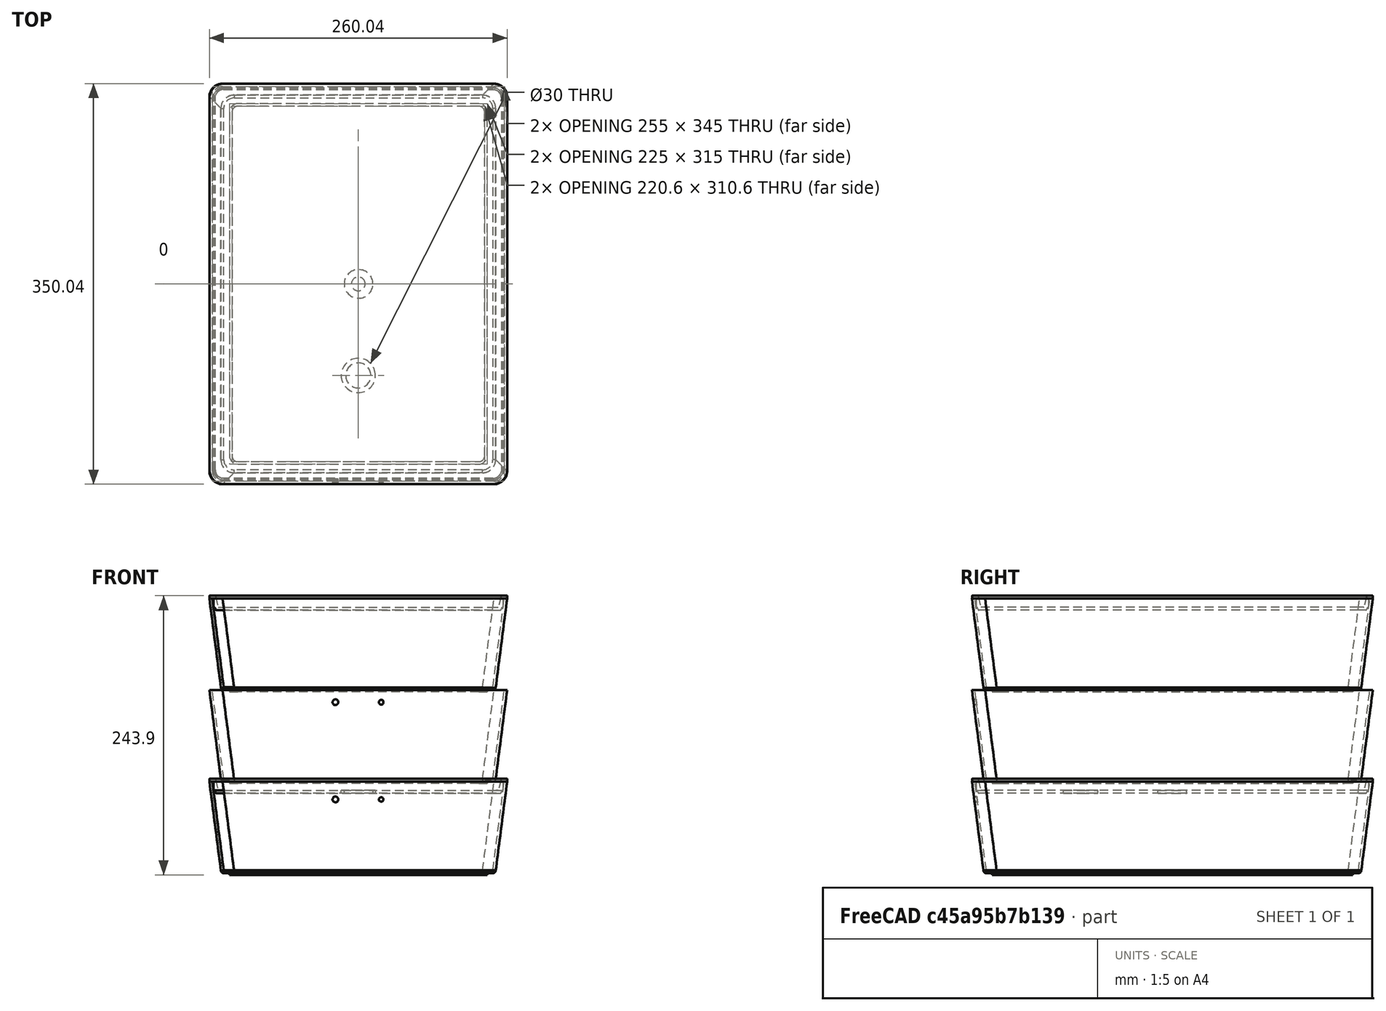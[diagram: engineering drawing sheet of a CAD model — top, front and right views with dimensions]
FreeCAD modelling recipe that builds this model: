
FCSTD DOCUMENT  (FreeCAD 0.16R6707 (Git))
Label: kuggis
License: All rights reserved
LicenseURL: http://en.wikipedia.org/wiki/All_rights_reserved
objects: Sketcher::SketchObject×10, Part::FeaturePython×6, PartDesign::Pad×3, Mesh::Feature×3, PartDesign::Pocket×3, Part::Feature×2, App::DocumentObjectGroup×2, Part::Cut×2, Part::Loft×1, Part::Thickness×1, Part::Sweep×1, Part::MultiFuse×1
note: 36 computed .brp shape members not serialized (recipe doc carries the construction recipe); baked Part::Feature solids carry a one-line shape summary decoded from their .brp

FEATURE [Sketcher::SketchObject] Sketch001  label="Lower"
  expr: Constraints[18] = Upper.Constraints.Depth - 20
  expr: Constraints[16] = Upper.Constraints.Width - 20
  sketch-geometry (8):
    g0: LineSegment StartX=-108.5 StartY=162.5 StartZ=0 EndX=108.5 EndY=162.5 EndZ=0
    g1: LineSegment StartX=117.5 StartY=153.5 StartZ=0 EndX=117.5 EndY=-153.5 EndZ=0
    g2: LineSegment StartX=108.5 StartY=-162.5 StartZ=0 EndX=-108.5 EndY=-162.5 EndZ=0
    g3: LineSegment StartX=-117.5 StartY=-153.5 StartZ=0 EndX=-117.5 EndY=153.5 EndZ=0
    g4: ArcOfCircle CenterX=-108.5 CenterY=153.5 CenterZ=0 NormalX=0 NormalY=0 NormalZ=1 Radius=9 StartAngle=1.5708 EndAngle=3.14159
    g5: ArcOfCircle CenterX=-108.5 CenterY=-153.5 CenterZ=0 NormalX=0 NormalY=0 NormalZ=1 Radius=9 StartAngle=3.14159 EndAngle=4.71239
    g6: ArcOfCircle CenterX=108.5 CenterY=-153.5 CenterZ=0 NormalX=0 NormalY=0 NormalZ=1 Radius=9 StartAngle=4.71239 EndAngle=6.28319
    g7: ArcOfCircle CenterX=108.5 CenterY=153.5 CenterZ=0 NormalX=0 NormalY=0 NormalZ=1 Radius=9 StartAngle=0 EndAngle=1.5708
  constraints (20):
    c: Horizontal(g0)
    c: Horizontal(g2)
    c: Vertical(g1)
    c: Tangent(g0,g4) = 1.5708
    c: Tangent(g3,g4) = 1.5708
    c: Tangent(g2,g5) = 1.5708
    c: Tangent(g3,g5) = 1.5708
    c: Tangent(g1,g6) = 1.5708
    c: Tangent(g2,g6) = 1.5708
    c: Tangent(g0,g7) = 1.5708
    c: Tangent(g1,g7) = 1.5708
    c: Equal(g4,g7)
    c: Equal(g7,g6)
    c: Equal(g6,g5)
    c: Symmetric(g0,g0,g-2)
    c: Symmetric(g3,g3,g-1)
    c: DistanceX(g3,g1) = 235
    c: Symmetric(g2,g0,g-1)
    c: DistanceY(g2,g0) = 325
    c: Radius(g4) = 9
FEATURE [Sketcher::SketchObject] Sketch002  label="Upper"
  Placement = pos=(0,0,77.5) rot=(0,0,1;0rad)
  sketch-geometry (8):
    g0: LineSegment StartX=-118.5 StartY=172.5 StartZ=0 EndX=118.5 EndY=172.5 EndZ=0
    g1: LineSegment StartX=127.5 StartY=163.5 StartZ=0 EndX=127.5 EndY=-163.5 EndZ=0
    g2: LineSegment StartX=118.5 StartY=-172.5 StartZ=0 EndX=-118.5 EndY=-172.5 EndZ=0
    g3: LineSegment StartX=-127.5 StartY=-163.5 StartZ=0 EndX=-127.5 EndY=163.5 EndZ=0
    g4: ArcOfCircle CenterX=-118.5 CenterY=163.5 CenterZ=0 NormalX=0 NormalY=0 NormalZ=1 Radius=9 StartAngle=1.5708 EndAngle=3.14159
    g5: ArcOfCircle CenterX=-118.5 CenterY=-163.5 CenterZ=0 NormalX=0 NormalY=0 NormalZ=1 Radius=9 StartAngle=3.14159 EndAngle=4.71239
    g6: ArcOfCircle CenterX=118.5 CenterY=-163.5 CenterZ=0 NormalX=0 NormalY=0 NormalZ=1 Radius=9 StartAngle=4.71239 EndAngle=6.28319
    g7: ArcOfCircle CenterX=118.5 CenterY=163.5 CenterZ=0 NormalX=0 NormalY=0 NormalZ=1 Radius=9 StartAngle=0 EndAngle=1.5708
  constraints (20):
    c: Horizontal(g0)
    c: Horizontal(g2)
    c: Vertical(g1)
    c: Vertical(g3)
    c: Tangent(g0,g4) = 1.5708
    c: Tangent(g3,g4) = 1.5708
    c: Tangent(g2,g5) = 1.5708
    c: Tangent(g3,g5) = 1.5708
    c: Tangent(g1,g6) = 1.5708
    c: Tangent(g2,g6) = 1.5708
    c: Tangent(g0,g7) = 1.5708
    c: Tangent(g1,g7) = 1.5708
    c: DistanceY(g2,g0) = 345  'Depth'
    c: DistanceX(g3,g1) = 255  'Width'
    c: Symmetric(g0,g0,g-2)
    c: Symmetric(g3,g3,g-1)
    c: Equal(g6,g7)
    c: Equal(g7,g5)
    c: Equal(g5,g4)
    c: Radius(g4) = 9  'CornerRadius'
FEATURE [Part::Loft] Loft
  Closed = false
  Ruled = false
  Sections = -> [Sketch001,Sketch002]
  Solid = true
FEATURE [Part::Thickness] Thickness001
  Faces = -> Loft [Face10]
  Intersection = false
  Join = 0
  Mode = 0
  SelfIntersection = false
  Value = 2.5
FEATURE [Sketcher::SketchObject] Sketch003  label="BottomDistanceSketch"
  Placement = pos=(0,0,-2.5) rot=(1,0,0;3.14159rad)
  Support = -> Thickness001 [Face20]
  sketch-geometry (16):
    g0: LineSegment StartX=-105.3 StartY=155.3 StartZ=0 EndX=105.3 EndY=155.3 EndZ=0
    g1: LineSegment StartX=110.3 StartY=150.3 StartZ=0 EndX=110.3 EndY=-150.3 EndZ=0
    g2: LineSegment StartX=105.3 StartY=-155.3 StartZ=0 EndX=-105.3 EndY=-155.3 EndZ=0
    g3: LineSegment StartX=-110.3 StartY=-150.3 StartZ=0 EndX=-110.3 EndY=150.3 EndZ=0
    g4: ArcOfCircle CenterX=-105.3 CenterY=150.3 CenterZ=0 NormalX=0 NormalY=0 NormalZ=1 Radius=5 StartAngle=1.5708 EndAngle=3.14159
    g5: ArcOfCircle CenterX=105.3 CenterY=150.3 CenterZ=0 NormalX=0 NormalY=0 NormalZ=1 Radius=5 StartAngle=0 EndAngle=1.5708
    g6: ArcOfCircle CenterX=105.3 CenterY=-150.3 CenterZ=0 NormalX=0 NormalY=0 NormalZ=1 Radius=5 StartAngle=4.71239 EndAngle=6.28319
    g7: ArcOfCircle CenterX=-105.3 CenterY=-150.3 CenterZ=0 NormalX=0 NormalY=0 NormalZ=1 Radius=5 StartAngle=3.14159 EndAngle=4.71239
    g8: LineSegment StartX=-105.3 StartY=157.5 StartZ=0 EndX=105.3 EndY=157.5 EndZ=0
    g9: LineSegment StartX=112.5 StartY=150.3 StartZ=0 EndX=112.5 EndY=-150.3 EndZ=0
    g10: LineSegment StartX=105.3 StartY=-157.5 StartZ=0 EndX=-105.3 EndY=-157.5 EndZ=0
    g11: LineSegment StartX=-112.5 StartY=-150.3 StartZ=0 EndX=-112.5 EndY=150.3 EndZ=0
    g12: ArcOfCircle CenterX=-105.3 CenterY=150.3 CenterZ=0 NormalX=0 NormalY=0 NormalZ=1 Radius=7.2 StartAngle=1.5708 EndAngle=3.14159
    g13: ArcOfCircle CenterX=105.3 CenterY=150.3 CenterZ=0 NormalX=0 NormalY=0 NormalZ=1 Radius=7.2 StartAngle=0 EndAngle=1.5708
    g14: ArcOfCircle CenterX=105.3 CenterY=-150.3 CenterZ=0 NormalX=0 NormalY=0 NormalZ=1 Radius=7.2 StartAngle=4.71239 EndAngle=6.28319
    g15: ArcOfCircle CenterX=-105.3 CenterY=-150.3 CenterZ=0 NormalX=0 NormalY=0 NormalZ=1 Radius=7.2 StartAngle=3.14159 EndAngle=4.71239
  constraints (36):
    c: Horizontal(g0)
    c: Horizontal(g2)
    c: Tangent(g0,g4) = 1.5708
    c: Tangent(g3,g4) = 1.5708
    c: Tangent(g0,g5) = 1.5708
    c: Tangent(g1,g5) = 1.5708
    c: Tangent(g1,g6) = 1.5708
    c: Tangent(g2,g6) = 1.5708
    c: Tangent(g2,g7) = 1.5708
    c: Tangent(g3,g7) = 1.5708
    c: Equal(g5,g6)
    c: Equal(g6,g7)
    c: Equal(g7,g4)
    c: Vertical(g11)
    c: Tangent(g8,g12) = 1.5708
    c: Tangent(g11,g12) = 1.5708
    c: Tangent(g8,g13) = 1.5708
    c: Tangent(g9,g13) = 1.5708
    c: Tangent(g9,g14) = 1.5708
    c: Tangent(g10,g14) = 1.5708
    c: Tangent(g10,g15) = 1.5708
    c: Tangent(g11,g15) = 1.5708
    c: Symmetric(g8,g8,g-2)
    c: Symmetric(g9,g9,g-1)
    c: DistanceX(g1,g9) = 2.2  'DistanceWidth'
    c: Equal(g14,g13)
    c: Equal(g13,g12)
    c: Equal(g12,g15)
    c: Symmetric(g10,g10,g-2)
    c: Coincident(g6,g14)
    c: Vertical(g3)
    c: Coincident(g15,g7)
    c: Coincident(g5,g13)
    c: Radius(g6) = 5
    c: DistanceY(g10,g8) = 315
    c: DistanceX(g11,g9) = 225
FEATURE [PartDesign::Pad] Pad002  label="BottomDistance"
  Length = 1.4
  Length2 = 100
  Sketch = -> Sketch003
  Type = 0
FEATURE [Part::FeaturePython] Clone  label="Bottom bottom"  # Draft clone (typed FeaturePython)
  Objects = -> [Pad002]
  Scale = (1,1,1)
FEATURE [Sketcher::SketchObject] Sketch  label="lidpath"
  Placement = pos=(0,0,75) rot=(0,0,1;0rad)
  expr: Constraints[19] = Upper.Constraints.CornerRadius
  expr: Constraints[15] = Upper.Constraints.Depth - 2
  expr: Constraints[14] = Upper.Constraints.Width - 2
  sketch-geometry (8):
    g0: LineSegment StartX=-117.5 StartY=171.5 StartZ=0 EndX=117.5 EndY=171.5 EndZ=0
    g1: LineSegment StartX=126.5 StartY=162.5 StartZ=0 EndX=126.5 EndY=-162.5 EndZ=0
    g2: LineSegment StartX=117.5 StartY=-171.5 StartZ=0 EndX=-117.5 EndY=-171.5 EndZ=0
    g3: LineSegment StartX=-126.5 StartY=-162.5 StartZ=0 EndX=-126.5 EndY=162.5 EndZ=0
    g4: ArcOfCircle CenterX=-117.5 CenterY=162.5 CenterZ=0 NormalX=0 NormalY=0 NormalZ=1 Radius=9 StartAngle=1.5708 EndAngle=3.14159
    g5: ArcOfCircle CenterX=117.5 CenterY=162.5 CenterZ=0 NormalX=0 NormalY=0 NormalZ=1 Radius=9 StartAngle=0 EndAngle=1.5708
    g6: ArcOfCircle CenterX=117.5 CenterY=-162.5 CenterZ=0 NormalX=0 NormalY=0 NormalZ=1 Radius=9 StartAngle=4.71239 EndAngle=6.28319
    g7: ArcOfCircle CenterX=-117.5 CenterY=-162.5 CenterZ=0 NormalX=0 NormalY=0 NormalZ=1 Radius=9 StartAngle=3.14159 EndAngle=4.71239
  constraints (20):
    c: Horizontal(g0)
    c: Horizontal(g2)
    c: Vertical(g1)
    c: Vertical(g3)
    c: Tangent(g0,g4) = 1.5708
    c: Tangent(g3,g4) = 1.5708
    c: Tangent(g0,g5) = 1.5708
    c: Tangent(g1,g5) = 1.5708
    c: Tangent(g1,g6) = 1.5708
    c: Tangent(g2,g6) = 1.5708
    c: Tangent(g2,g7) = 1.5708
    c: Tangent(g3,g7) = 1.5708
    c: Symmetric(g0,g0,g-2)
    c: Symmetric(g1,g1,g-1)
    c: DistanceX(g3,g1) = 253
    c: DistanceY(g2,g0) = 343
    c: Equal(g7,g6)
    c: Equal(g6,g5)
    c: Equal(g5,g4)
    c: Radius(g4) = 9
FEATURE [Sketcher::SketchObject] Sketch013  label="lid-profile"
  Placement = pos=(0,0,0) rot=(-1,0,0;4.71239rad)
  sketch-geometry (17):
    g0: LineSegment StartX=120.4 StartY=67.5 StartZ=0 EndX=123.961 EndY=67.5 EndZ=0
    g1: LineSegment StartX=127.5 StartY=77.5 StartZ=0 EndX=129.9 EndY=77.5 EndZ=0
    g2: LineSegment StartX=130 StartY=77.6 StartZ=0 EndX=130 EndY=79.9 EndZ=0
    g3: LineSegment StartX=129.9 StartY=80 StartZ=0 EndX=125.576 EndY=80 EndZ=0
    g4: LineSegment StartX=124.605 StartY=79.2413 StartZ=0 EndX=122.327 EndY=70.0759 EndZ=0
    g5: LineSegment StartX=122.23 StartY=70 StartZ=0 EndX=120.4 EndY=70 EndZ=0
    g6: LineSegment StartX=120.4 StartY=70 StartZ=0 EndX=120.4 EndY=67.5 EndZ=0
    g7: LineSegment StartX=126.5 StartY=76.5 StartZ=0 EndX=126.5 EndY=70.7588 EndZ=0
    g8: ArcOfCircle CenterX=125.5 CenterY=70.7588 CenterZ=0 NormalX=0 NormalY=0 NormalZ=1 Radius=1 StartAngle=4.93286 EndAngle=6.28319
    g9: ArcOfCircle CenterX=125.937 CenterY=68.8072 CenterZ=0 NormalX=0 NormalY=0 NormalZ=1 Radius=1 StartAngle=1.79126 EndAngle=3.29581
    g10: ArcOfCircle CenterX=123.961 CenterY=68.5 CenterZ=0 NormalX=0 NormalY=0 NormalZ=1 Radius=1 StartAngle=4.71239 EndAngle=6.43741
    g11: ArcOfCircle CenterX=122.23 CenterY=70.1 CenterZ=0 NormalX=0 NormalY=0 NormalZ=1 Radius=0.1 StartAngle=4.71239 EndAngle=6.03952
    g12: ArcOfCircle CenterX=125.576 CenterY=79 CenterZ=0 NormalX=0 NormalY=0 NormalZ=1 Radius=1 StartAngle=1.5708 EndAngle=2.89792
    g13: ArcOfCircle CenterX=129.9 CenterY=77.6 CenterZ=0 NormalX=0 NormalY=0 NormalZ=1 Radius=0.1 StartAngle=4.71239 EndAngle=6.28319
    g14: ArcOfCircle CenterX=129.9 CenterY=79.9 CenterZ=0 NormalX=0 NormalY=0 NormalZ=1 Radius=0.1 StartAngle=0 EndAngle=1.5708
    g15: ArcOfCircle CenterX=127.5 CenterY=76.5 CenterZ=0 NormalX=0 NormalY=0 NormalZ=1 Radius=1 StartAngle=1.5708 EndAngle=3.14159
    g16: LineSegment [constr] StartX=126.5 StartY=76.5 StartZ=0 EndX=124.074 EndY=77.1032 EndZ=0
  constraints (45):
    c: Horizontal(g0)
    c: Coincident(g5,g6)
    c: Coincident(g6,g0)
    c: Horizontal(g5)
    c: Horizontal(g3)
    c: Vertical(g2)
    c: Horizontal(g1)
    c: Vertical(g6)
    c: DistanceY(g6,g6) = 2.5
    c: Vertical(g7)
    c: Coincident(g8,g7)
    c: Coincident(g9,g8)
    c: Coincident(g10,g9)
    c: Coincident(g0,g10)
    c: Tangent(g10,g9)
    c: Tangent(g9,g8)
    c: Tangent(g8,g7)
    c: Tangent(g0,g10)
    c: Tangent(g5,g11) = 1.5708
    c: Tangent(g4,g11) = 1.5708
    c: Tangent(g4,g12) = -1.5708
    c: Tangent(g3,g12) = -1.5708
    c: Tangent(g1,g13) = -1.5708
    c: Tangent(g2,g13) = -1.5708
    c: Tangent(g2,g14) = -1.5708
    c: Tangent(g3,g14) = -1.5708
    c: Tangent(g7,g15) = -1.5708
    c: Tangent(g1,g15) = 1.5708
    c: DistanceY(g1,g3) = 2.5
    c: Equal(g11,g13)
    c: Equal(g13,g14)
    c: Radius(g11) = 0.1
    c: Equal(g9,g8)
    c: Equal(g8,g10)
    c: Radius(g10) = 1
    c: Radius(g15) = 1
    c: Radius(g12) = 1
    c: DistanceY(g5,g3) = 10
    c: DistanceX(g7,g2) = 3.5
    c: DistanceY(g3) = 80
    c: Coincident(g16,g7)
    c: PointOnObject(g16,g4)
    c: Perpendicular(g16,g4)
    c: Distance(g16) = 2.5
    c: DistanceX(g2) = 130
FEATURE [Part::Sweep] Sweep  label="lidSweep"
  Frenet = false
  Sections = -> [Sketch013]
  Solid = false
  Spine = -> Sketch [Edge5,Edge6,Edge7,Edge8,Edge1,Edge2,Edge3,Edge4]
  Transition = 1
FEATURE [Sketcher::SketchObject] Sketch014
  Placement = pos=(0,0,67.5) rot=(0,0,1;0rad)
  sketch-geometry (4):
    g0: LineSegment StartX=-120.5 StartY=165.5 StartZ=0 EndX=120.5 EndY=165.5 EndZ=0
    g1: LineSegment StartX=120.5 StartY=165.5 StartZ=0 EndX=120.5 EndY=-165.5 EndZ=0
    g2: LineSegment StartX=120.5 StartY=-165.5 StartZ=0 EndX=-120.5 EndY=-165.5 EndZ=0
    g3: LineSegment StartX=-120.5 StartY=-165.5 StartZ=0 EndX=-120.5 EndY=165.5 EndZ=0
  constraints (12):
    c: Coincident(g0,g1)
    c: Coincident(g1,g2)
    c: Coincident(g2,g3)
    c: Coincident(g3,g0)
    c: Horizontal(g0)
    c: Horizontal(g2)
    c: Vertical(g1)
    c: Vertical(g3)
    c: Symmetric(g0,g0,g-2)
    c: Symmetric(g0,g1,g-1)
    c: DistanceX(g0,g0) = 241
    c: DistanceY(g3,g3) = 331
FEATURE [PartDesign::Pad] Pad
  Length = 2.5
  Length2 = 100
  Placement = pos=(0,0,67.5) rot=(0,0,1;0rad)
  Sketch = -> Sketch014
  Type = 0
FEATURE [Part::Feature] Sweep_solid  label="Sweep (Solid)"
  shape: bbox 262.1 x 352.1 x 12.5 mm, 128 faces (baked)
FEATURE [Part::MultiFuse] Fusion
  Shapes = -> [Pad,Sweep_solid]
FEATURE [App::DocumentObjectGroup] Group  label="Box"
  Group = -> [Pad002,Thickness001,Sketch,Sweep,Fusion]
FEATURE [Part::Feature] Fusion001  label="Lid Bottom"
  shape: bbox 262.1 x 352.1 x 12.5 mm, 92 faces (baked)
FEATURE [Part::FeaturePython] Clone001  label="Lid center"  # Draft clone (typed FeaturePython)
  Objects = -> [Fusion001]
  Placement = pos=(0,0,80) rot=(0,0,1;0rad)
  Scale = (1,1,1)
FEATURE [Part::FeaturePython] Clone002  label="Lid top"  # Draft clone (typed FeaturePython)
  Objects = -> [Clone001]
  Placement = pos=(0,0,160) rot=(0,0,1;0rad)
  Scale = (1,1,1)
FEATURE [Part::FeaturePython] Clone003  label="Bottom center"  # Draft clone (typed FeaturePython)
  Objects = -> [Clone]
  Placement = pos=(0,0,80) rot=(0,0,1;0rad)
  Scale = (1,1,1)
FEATURE [Part::FeaturePython] Clone004  label="Box top"  # Draft clone (typed FeaturePython)
  Objects = -> [Clone003]
  Placement = pos=(0,0,160) rot=(0,0,1;0rad)
  Scale = (1,1,1)
FEATURE [Sketcher::SketchObject] Sketch015  label="lid-top"
  Placement = pos=(0,0,230) rot=(0,0,1;0rad)
  Support = -> Clone002 [Face50]
  sketch-geometry (6):
    g0: Circle CenterX=0 CenterY=-80 CenterZ=0 NormalX=0 NormalY=0 NormalZ=1 Radius=23
    g1: Circle CenterX=0 CenterY=80 CenterZ=0 NormalX=0 NormalY=0 NormalZ=1 Radius=40.5
    g2: LineSegment StartX=-130 StartY=-175 StartZ=0 EndX=130 EndY=-175 EndZ=0
    g3: LineSegment StartX=130 StartY=-175 StartZ=0 EndX=130 EndY=175 EndZ=0
    g4: LineSegment StartX=130 StartY=175 StartZ=0 EndX=-130 EndY=175 EndZ=0
    g5: LineSegment StartX=-130 StartY=175 StartZ=0 EndX=-130 EndY=-175 EndZ=0
  constraints (18):
    c: PointOnObject(g0,g-2)
    c: PointOnObject(g1,g-2)
    c: Radius(g0) = 23
    c: Radius(g1) = 40.5
    c: Symmetric(g0,g1,g-1)
    c: DistanceY(g-1,g1) = 80
    c: Coincident(g2,g3)
    c: Coincident(g3,g4)
    c: Coincident(g4,g5)
    c: Coincident(g5,g2)
    c: Horizontal(g2)
    c: Horizontal(g4)
    c: Vertical(g3)
    c: Vertical(g5)
    c: Symmetric(g3,g2,g-1)
    c: Symmetric(g4,g3,g-2)
    c: DistanceX(g4,g4) = 260
    c: DistanceY(g3,g3) = 350
FEATURE [Mesh::Feature] Dome_50_with_penises
  Placement = pos=(0,-80,160) rot=(0,0,1;0rad)
FEATURE [Mesh::Feature] threaded_standpipe_22mm_doubledribble
  Placement = pos=(0,-80,160) rot=(0,0,1;0rad)
FEATURE [Sketcher::SketchObject] Sketch016  label="box-top"
  Placement = pos=(0,0,160) rot=(0,0,1;0rad)
  Support = -> Clone004 [Face2]
  sketch-geometry (6):
    g0: Circle CenterX=0 CenterY=-80 CenterZ=0 NormalX=0 NormalY=0 NormalZ=1 Radius=11
    g1: Circle CenterX=0 CenterY=0 CenterZ=0 NormalX=0 NormalY=0 NormalZ=1 Radius=6
    g2: LineSegment StartX=-130 StartY=175 StartZ=0 EndX=130 EndY=175 EndZ=0
    g3: LineSegment StartX=130 StartY=175 StartZ=0 EndX=130 EndY=-175 EndZ=0
    g4: LineSegment StartX=130 StartY=-175 StartZ=0 EndX=-130 EndY=-175 EndZ=0
    g5: LineSegment StartX=-130 StartY=-175 StartZ=0 EndX=-130 EndY=175 EndZ=0
  constraints (17):
    c: PointOnObject(g0,g-2)
    c: Radius(g0) = 11
    c: DistanceY(g0) = -80
    c: Coincident(g1,g-1)
    c: Radius(g1) = 6
    c: Coincident(g2,g3)
    c: Coincident(g3,g4)
    c: Coincident(g4,g5)
    c: Coincident(g5,g2)
    c: Horizontal(g2)
    c: Horizontal(g4)
    c: Vertical(g3)
    c: Vertical(g5)
    c: Symmetric(g3,g2,g-1)
    c: Symmetric(g2,g2,g-2)
    c: DistanceX(g2,g2) = 260
    c: DistanceY(g3,g3) = 350
FEATURE [PartDesign::Pocket] Pocket001
  Length = 5
  Placement = pos=(0,0,160) rot=(0,0,1;0rad)
  Sketch = -> Sketch016
  Type = 2
FEATURE [Sketcher::SketchObject] Sketch017  label="lid-center001"
  Placement = pos=(0,0,150) rot=(0,0,1;0rad)
  Support = -> Clone001 [Face50]
  sketch-geometry (6):
    g0: Circle CenterX=0 CenterY=-80 CenterZ=0 NormalX=0 NormalY=0 NormalZ=1 Radius=15
    g1: Circle CenterX=0.266379 CenterY=0 CenterZ=0 NormalX=0 NormalY=0 NormalZ=1 Radius=12.5
    g2: LineSegment StartX=-130 StartY=175 StartZ=0 EndX=130 EndY=175 EndZ=0
    g3: LineSegment StartX=130 StartY=175 StartZ=0 EndX=130 EndY=-175 EndZ=0
    g4: LineSegment StartX=130 StartY=-175 StartZ=0 EndX=-130 EndY=-175 EndZ=0
    g5: LineSegment StartX=-130 StartY=-175 StartZ=0 EndX=-130 EndY=175 EndZ=0
  constraints (17):
    c: PointOnObject(g0,g-2)
    c: PointOnObject(g1,g-1)
    c: Radius(g0) = 15
    c: Radius(g1) = 12.5
    c: DistanceY(g0) = -80
    c: Coincident(g2,g3)
    c: Coincident(g3,g4)
    c: Coincident(g4,g5)
    c: Coincident(g5,g2)
    c: Horizontal(g2)
    c: Horizontal(g4)
    c: Vertical(g3)
    c: Vertical(g5)
    c: Symmetric(g2,g3,g-1)
    c: Symmetric(g2,g2,g-2)
    c: DistanceX(g2,g2) = 260
    c: DistanceY(g3,g3) = 350
FEATURE [PartDesign::Pocket] Pocket002  label="lid-center"
  Length = 5
  Placement = pos=(0,0,80) rot=(0,0,1;0rad)
  Sketch = -> Sketch017
  Type = 2
FEATURE [Mesh::Feature] nut_22mm
  Placement = pos=(0,-80,134) rot=(0,0,1;0rad)
FEATURE [Sketcher::SketchObject] Sketch018
  Placement = pos=(0,-200,0) rot=(-1,0,0;4.71239rad)
  sketch-geometry (2):
    g0: Circle CenterX=-20 CenterY=147 CenterZ=0 NormalX=0 NormalY=0 NormalZ=1 Radius=2.5
    g1: Circle CenterX=20 CenterY=147 CenterZ=0 NormalX=0 NormalY=0 NormalZ=1 Radius=2
  constraints (5):
    c: Radius(g0) = 2.5
    c: Radius(g1) = 2
    c: Symmetric(g0,g1,g-2)
    c: DistanceY(g0) = 147
    c: DistanceX(g0) = -20
FEATURE [PartDesign::Pad] Pad003
  Length = 40
  Length2 = 100
  Placement = pos=(0,-200,0) rot=(-1,0,0;4.71239rad)
  Reversed = true
  Sketch = -> Sketch018
  Type = 0
FEATURE [Part::Cut] Cut  label="Box ceter"
  Base = -> Clone003
  Tool = -> Pad003
FEATURE [Part::FeaturePython] Clone005  label="wires"  # Draft clone (typed FeaturePython)
  Objects = -> [Pad003]
  Placement = pos=(0,-200,-85) rot=(-1,0,0;4.71239rad)
  Scale = (1,1,1)
FEATURE [Part::Cut] Cut001  label="Box bottom"
  Base = -> Clone
  Tool = -> Clone005
FEATURE [PartDesign::Pocket] Pocket
  Length = 5
  Placement = pos=(0,0,160) rot=(0,0,1;0rad)
  Sketch = -> Sketch015
  Type = 2
FEATURE [App::DocumentObjectGroup] Group001  label="Siphen"
  Group = -> [Dome_50_with_penises,threaded_standpipe_22mm_doubledribble,nut_22mm]
